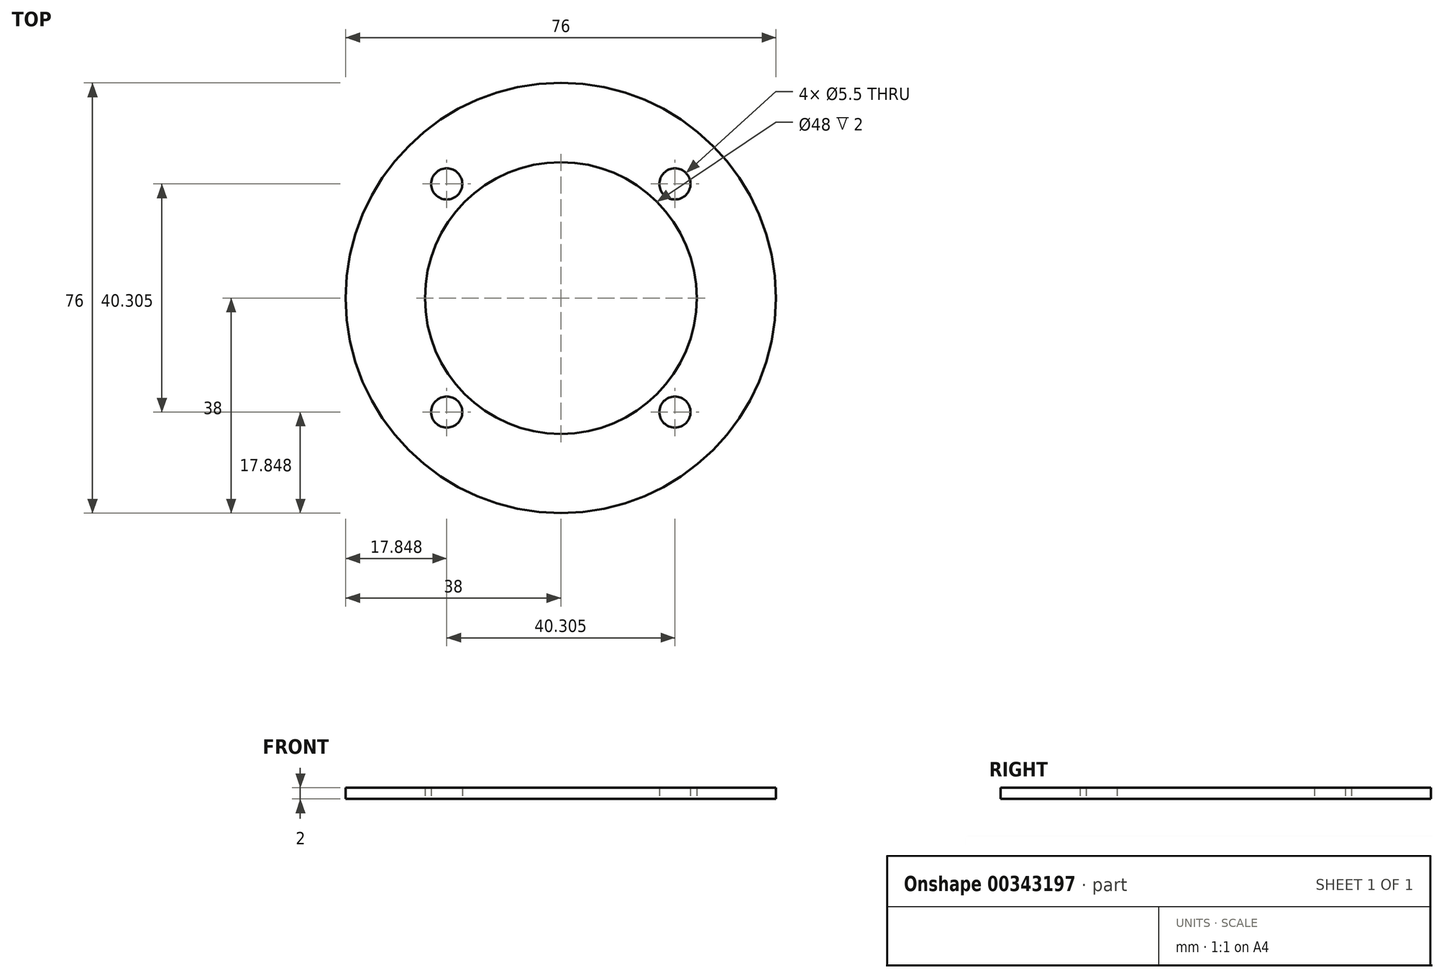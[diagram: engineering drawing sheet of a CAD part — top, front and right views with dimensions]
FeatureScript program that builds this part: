
annotation { "Feature Type Name" : "Feature", "Feature Type Description" : "" }
export const myFeature = defineFeature(function(context is Context, id is Id, definition is map)
    precondition{}
    {
        {
            var Q0;
            Q0=qCreatedBy(makeId("Top.planeOp"),FACE);
            var sketch = newSketch(context, id + "F0", { "sketchPlane" : qUnion([Q0])});
            skLineSegment(sketch, "E0.bottom", {"start": v(22, -25) * mm, "end": v(-22, -25) * mm});
            skLineSegment(sketch, "E0.top", {"start": v(22, 25) * mm, "end": v(-22, 25) * mm});
            skLineSegment(sketch, "E0.left", {"start": v(25, -22) * mm, "end": v(25, 22) * mm});
            skLineSegment(sketch, "E0.right", {"start": v(-25, -22) * mm, "end": v(-25, 22) * mm});
            skPoint(sketch, "E0.middle", {"position": v(0, 0) * mm});
            skPoint(sketch, "E1.visualSharp", {"position": v(25, 25) * mm});
            skArc(sketch, "E1.filletArc", {"start": v(25, 22) * mm, "mid": v(24.12, 24.12) * mm, "end": v(22, 25) * mm});
            skPoint(sketch, "E2.visualSharp", {"position": v(25, -25) * mm});
            skArc(sketch, "E2.filletArc", {"start": v(22, -25) * mm, "mid": v(24.12, -24.12) * mm, "end": v(25, -22) * mm});
            skPoint(sketch, "E3.visualSharp", {"position": v(-25, -25) * mm});
            skArc(sketch, "E3.filletArc", {"start": v(-25, -22) * mm, "mid": v(-24.12, -24.12) * mm, "end": v(-22, -25) * mm});
            skPoint(sketch, "E4.visualSharp", {"position": v(-25, 25) * mm});
            skArc(sketch, "E4.filletArc", {"start": v(-22, 25) * mm, "mid": v(-24.12, 24.12) * mm, "end": v(-25, 22) * mm});
            skSolve(sketch);
        }
        {
            var Q0;
            Q0=qCreatedBy(makeId("Top.planeOp"),FACE);
            var sketch = newSketch(context, id + "F1", { "sketchPlane" : qUnion([Q0])});
            skCircle(sketch, "E5", {"center": v(0, 0) * mm, "radius": 38 * mm});
            skCircle(sketch, "E6", {"center": v(0, 0) * mm, "radius": 24 * mm});
            skPoint(sketch, "E7.0.end.orphan", {"position": v(-22, 25) * mm});
            skPoint(sketch, "E7.0.start.orphan", {"position": v(22, 25) * mm});
            skPoint(sketch, "E7.3.end.orphan", {"position": v(-25, 22) * mm});
            skPoint(sketch, "E7.3.start.orphan", {"position": v(-22, 25) * mm});
            skPoint(sketch, "E7.1.end.orphan", {"position": v(-25, 22) * mm});
            skPoint(sketch, "E7.1.start.orphan", {"position": v(-25, -22) * mm});
            skPoint(sketch, "E7.7.end.orphan", {"position": v(-22, -25) * mm});
            skPoint(sketch, "E7.7.start.orphan", {"position": v(-25, -22) * mm});
            skPoint(sketch, "E7.6.end.orphan", {"position": v(-22, -25) * mm});
            skPoint(sketch, "E7.6.start.orphan", {"position": v(22, -25) * mm});
            skPoint(sketch, "E7.5.end.orphan", {"position": v(25, -22) * mm});
            skPoint(sketch, "E7.5.start.orphan", {"position": v(22, -25) * mm});
            skPoint(sketch, "E7.2.end.orphan", {"position": v(25, 22) * mm});
            skPoint(sketch, "E7.2.start.orphan", {"position": v(25, -22) * mm});
            skPoint(sketch, "E7.4.end.orphan", {"position": v(22, 25) * mm});
            skPoint(sketch, "E7.4.start.orphan", {"position": v(25, 22) * mm});
            skLineSegment(sketch, "E8", {"start": v(0, 0) * mm, "end": v(-26.87, 26.87) * mm, "construction": true});
            skCircle(sketch, "E9", {"center": v(-20.15, 20.15) * mm, "radius": 2.75 * mm});
            skCircle(sketch, "E10.1.0", {"center": v(-20.15, -20.15) * mm, "radius": 2.75 * mm});
            skCircle(sketch, "E10.2.0", {"center": v(20.15, -20.15) * mm, "radius": 2.75 * mm});
            skCircle(sketch, "E10.3.0", {"center": v(20.15, 20.15) * mm, "radius": 2.75 * mm});
            skSolve(sketch);
        }
        {
            var Q0;
            Q0=makeQuery(id+"F1.imprint","IMPRINT",FACE,{"disambiguationData":[TD([[makeQuery(id+"F1.imprint","IMPRINT",EDGE,{"derivedFrom":sQuery(id+"F1.wireOp",EDGE,"E5")}),1.0]])]});
            extrude(context, id + "F2", {"entities" : qUnion([Q0]), "depth" : 2 * mm});
        }
    });
